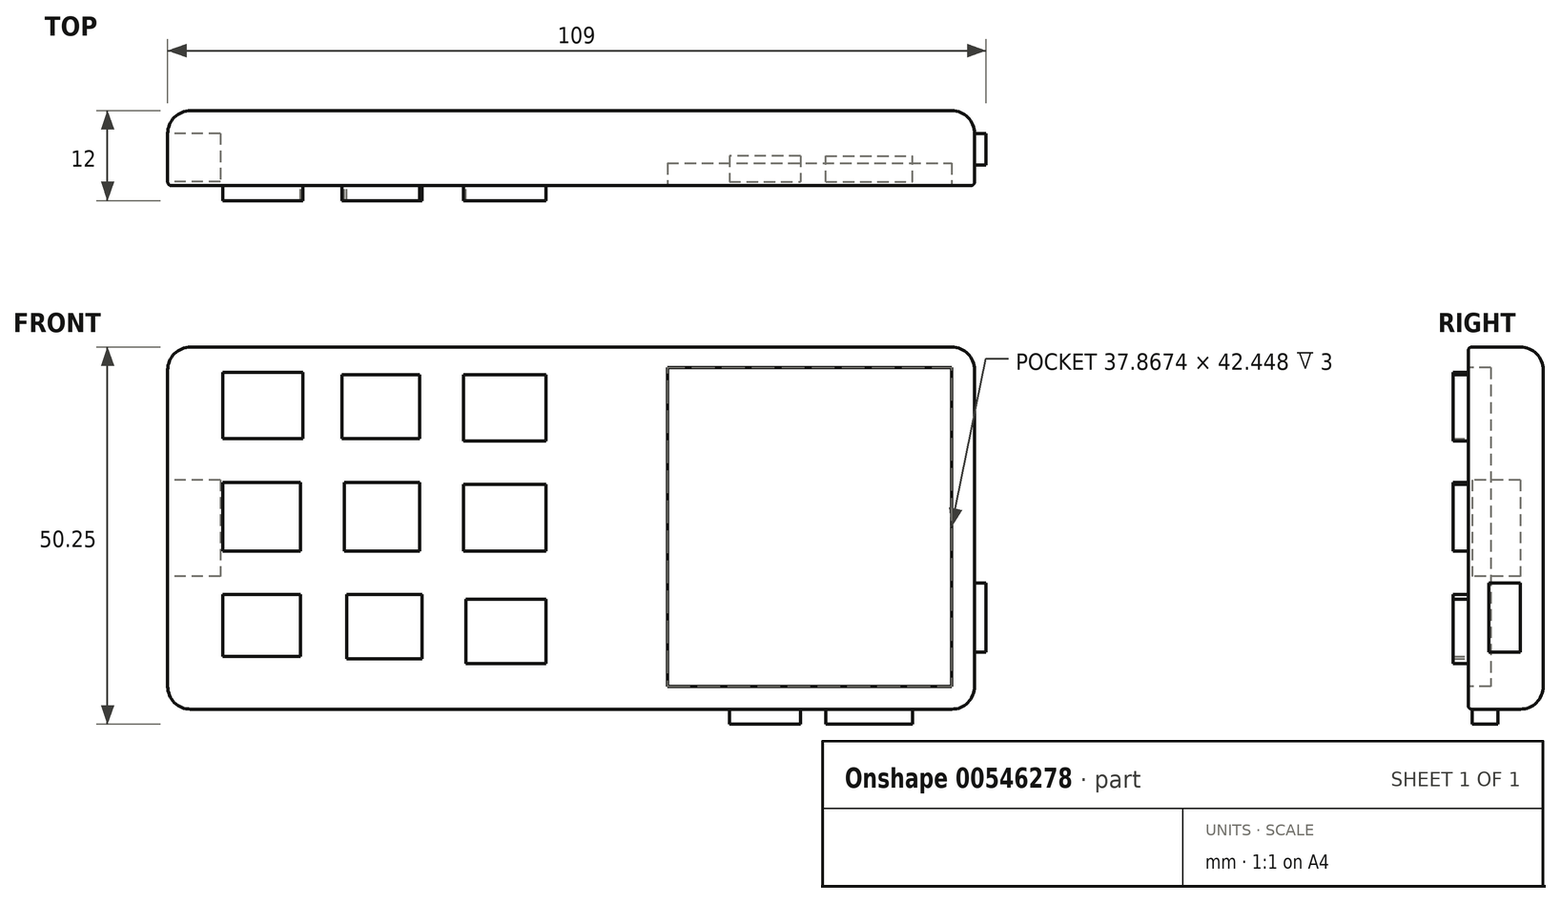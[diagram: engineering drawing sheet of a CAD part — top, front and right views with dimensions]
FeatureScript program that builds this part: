
annotation { "Feature Type Name" : "Feature", "Feature Type Description" : "" }
export const myFeature = defineFeature(function(context is Context, id is Id, definition is map)
    precondition{}
    {
        {
            var Q0;
            Q0=qCreatedBy(makeId("Front.planeOp"),FACE);
            var sketch = newSketch(context, id + "F0", { "sketchPlane" : qUnion([Q0])});
            skLineSegment(sketch, "E0.bottom", {"start": v(-50.39, 27.18) * mm, "end": v(57.1, 27.18) * mm});
            skLineSegment(sketch, "E0.top", {"start": v(-50.39, -21.07) * mm, "end": v(57.1, -21.07) * mm});
            skLineSegment(sketch, "E0.left", {"start": v(-50.39, 27.18) * mm, "end": v(-50.39, -21.07) * mm});
            skLineSegment(sketch, "E0.right", {"start": v(57.1, 27.18) * mm, "end": v(57.1, -21.07) * mm});
            skSolve(sketch);
        }
        {
            var Q0;
            Q0=makeQuery(id+"F0.imprint","IMPRINT",FACE,{"disambiguationData":[TD([[makeQuery(id+"F0.imprint","IMPRINT",EDGE,{"derivedFrom":sQuery(id+"F0.wireOp",EDGE,"E0.bottom")}),-1.0]])]});
            extrude(context, id + "F1", {"entities" : qUnion([Q0]), "oppositeDirection" : true, "depth" : 10 * mm, "offsetDistance" : 25.4 * mm});
        }
        {
            var Q0;
            Q0=makeQuery(id+"F1.opExtrude","CAP_FACE",FACE,{"disambiguationData":[OSD([sQuery(id+"F0.wireOp",EDGE,"E0.bottom"),sQuery(id+"F0.wireOp",EDGE,"E0.top"),sQuery(id+"F0.wireOp",EDGE,"E0.left"),sQuery(id+"F0.wireOp",EDGE,"E0.right")])],"isStart":true});
            var sketch = newSketch(context, id + "F2", { "sketchPlane" : qUnion([Q0])});
            skLineSegment(sketch, "E1.bottom", {"start": v(16.19, 24.43) * mm, "end": v(54.05, 24.43) * mm});
            skLineSegment(sketch, "E1.top", {"start": v(16.19, -18.02) * mm, "end": v(54.05, -18.02) * mm});
            skLineSegment(sketch, "E1.left", {"start": v(16.19, 24.43) * mm, "end": v(16.19, -18.02) * mm});
            skLineSegment(sketch, "E1.right", {"start": v(54.05, 24.43) * mm, "end": v(54.05, -18.02) * mm});
            skSolve(sketch);
        }
        {
            var Q0;
            Q0=makeQuery(id+"F2.imprint","IMPRINT",FACE,{"disambiguationData":[TD([[makeQuery(id+"F2.imprint","IMPRINT",EDGE,{"derivedFrom":sQuery(id+"F2.wireOp",EDGE,"E1.bottom")}),-1.0]])]});
            extrude(context, id + "F3", {"entities" : qUnion([Q0]), "operationType" : NewBodyOperationType.REMOVE, "oppositeDirection" : true, "depth" : 3 * mm, "offsetDistance" : 25.4 * mm});
        }
        {
            var Q0;
            Q0=makeQuery(id+"F1.opExtrude","CAP_FACE",FACE,{"disambiguationData":[OSD([sQuery(id+"F0.wireOp",EDGE,"E0.bottom"),sQuery(id+"F0.wireOp",EDGE,"E0.top"),sQuery(id+"F0.wireOp",EDGE,"E0.left"),sQuery(id+"F0.wireOp",EDGE,"E0.right")])],"isStart":true});
            var sketch = newSketch(context, id + "F4", { "sketchPlane" : qUnion([Q0])});
            skLineSegment(sketch, "E2.bottom", {"start": v(0, 23.51) * mm, "end": v(-11, 23.51) * mm});
            skLineSegment(sketch, "E2.top", {"start": v(0, 14.66) * mm, "end": v(-11, 14.66) * mm});
            skLineSegment(sketch, "E2.left", {"start": v(0, 23.51) * mm, "end": v(0, 14.66) * mm});
            skLineSegment(sketch, "E2.right", {"start": v(-11, 23.51) * mm, "end": v(-11, 14.66) * mm});
            skLineSegment(sketch, "E3.bottom", {"start": v(0, 8.55) * mm, "end": v(-11, 8.55) * mm});
            skLineSegment(sketch, "E3.top", {"start": v(0, 0) * mm, "end": v(-11, 0) * mm});
            skLineSegment(sketch, "E3.left", {"start": v(0, 8.55) * mm, "end": v(0, 0) * mm});
            skLineSegment(sketch, "E3.right", {"start": v(-11, 8.55) * mm, "end": v(-11, 0) * mm});
            skLineSegment(sketch, "E4.bottom", {"start": v(0, -6.72) * mm, "end": v(-11, -6.72) * mm});
            skLineSegment(sketch, "E4.top", {"start": v(0, -14.96) * mm, "end": v(-11, -14.96) * mm});
            skLineSegment(sketch, "E4.left", {"start": v(0, -6.72) * mm, "end": v(0, -14.96) * mm});
            skLineSegment(sketch, "E4.right", {"start": v(-11, -6.72) * mm, "end": v(-11, -14.96) * mm});
            skLineSegment(sketch, "E5.bottom", {"start": v(-17.1, -6.72) * mm, "end": v(-28.1, -6.72) * mm});
            skLineSegment(sketch, "E5.top", {"start": v(-17.1, -14.96) * mm, "end": v(-28.1, -14.96) * mm});
            skLineSegment(sketch, "E5.left", {"start": v(-17.1, -6.72) * mm, "end": v(-17.1, -14.96) * mm});
            skLineSegment(sketch, "E5.right", {"start": v(-28.1, -6.72) * mm, "end": v(-28.1, -14.96) * mm});
            skLineSegment(sketch, "E6.bottom", {"start": v(-16.8, 0) * mm, "end": v(-28.1, 0) * mm});
            skLineSegment(sketch, "E6.top", {"start": v(-16.8, 8.55) * mm, "end": v(-28.1, 8.55) * mm});
            skLineSegment(sketch, "E6.left", {"start": v(-16.8, 0) * mm, "end": v(-16.8, 8.55) * mm});
            skLineSegment(sketch, "E6.right", {"start": v(-28.1, 0) * mm, "end": v(-28.1, 8.55) * mm});
            skLineSegment(sketch, "E7.bottom", {"start": v(-17.1, 14.66) * mm, "end": v(-28.1, 14.66) * mm});
            skLineSegment(sketch, "E7.top", {"start": v(-17.1, 23.82) * mm, "end": v(-28.1, 23.82) * mm});
            skLineSegment(sketch, "E7.left", {"start": v(-17.1, 14.66) * mm, "end": v(-17.1, 23.82) * mm});
            skLineSegment(sketch, "E7.right", {"start": v(-28.1, 14.66) * mm, "end": v(-28.1, 23.82) * mm});
            skLineSegment(sketch, "E8.bottom", {"start": v(-34.2, 23.82) * mm, "end": v(-44.59, 23.82) * mm});
            skLineSegment(sketch, "E8.top", {"start": v(-34.2, 14.66) * mm, "end": v(-44.59, 14.66) * mm});
            skLineSegment(sketch, "E8.left", {"start": v(-34.2, 23.82) * mm, "end": v(-34.2, 14.66) * mm});
            skLineSegment(sketch, "E8.right", {"start": v(-44.59, 23.82) * mm, "end": v(-44.59, 14.66) * mm});
            skLineSegment(sketch, "E9.bottom", {"start": v(-34.5, 8.55) * mm, "end": v(-44.59, 8.55) * mm});
            skLineSegment(sketch, "E9.top", {"start": v(-34.5, 0) * mm, "end": v(-44.59, 0) * mm});
            skLineSegment(sketch, "E9.left", {"start": v(-34.5, 8.55) * mm, "end": v(-34.5, 0) * mm});
            skLineSegment(sketch, "E9.right", {"start": v(-44.59, 8.55) * mm, "end": v(-44.59, 0) * mm});
            skLineSegment(sketch, "E10.bottom", {"start": v(-34.81, -6.72) * mm, "end": v(-44.59, -6.72) * mm});
            skLineSegment(sketch, "E10.top", {"start": v(-34.81, -14.96) * mm, "end": v(-44.59, -14.96) * mm});
            skLineSegment(sketch, "E10.left", {"start": v(-34.81, -6.72) * mm, "end": v(-34.81, -14.96) * mm});
            skLineSegment(sketch, "E10.right", {"start": v(-44.59, -6.72) * mm, "end": v(-44.59, -14.96) * mm});
            skSolve(sketch);
        }
        {
            var Q0;
            Q0=makeQuery(id+"F4.imprint","IMPRINT",FACE,{"disambiguationData":[TD([[makeQuery(id+"F4.imprint","IMPRINT",EDGE,{"derivedFrom":sQuery(id+"F4.wireOp",EDGE,"E2.bottom")}),1.0]])]});
            extrude(context, id + "F5", {"entities" : qUnion([Q0]), "operationType" : NewBodyOperationType.ADD, "depth" : 2 * mm, "offsetDistance" : 25.4 * mm});
        }
        {
            var Q0;
            Q0=makeQuery(id+"F1.opExtrude","CAP_FACE",FACE,{"disambiguationData":[OSD([sQuery(id+"F0.wireOp",EDGE,"E0.bottom"),sQuery(id+"F0.wireOp",EDGE,"E0.top"),sQuery(id+"F0.wireOp",EDGE,"E0.left"),sQuery(id+"F0.wireOp",EDGE,"E0.right")])],"isStart":true});
            var sketch = newSketch(context, id + "F6", { "sketchPlane" : qUnion([Q0])});
            skLineSegment(sketch, "E11.bottom", {"start": v(-11, 8.86) * mm, "end": v(0, 8.86) * mm});
            skLineSegment(sketch, "E11.top", {"start": v(-11, 0) * mm, "end": v(0, 0) * mm});
            skLineSegment(sketch, "E11.left", {"start": v(-11, 8.86) * mm, "end": v(-11, 0) * mm});
            skLineSegment(sketch, "E11.right", {"start": v(0, 8.86) * mm, "end": v(0, 0) * mm});
            skSolve(sketch);
        }
        {
            var Q0;
            Q0=makeQuery(id+"F6.imprint","IMPRINT",FACE,{"disambiguationData":[TD([[makeQuery(id+"F6.imprint","IMPRINT",EDGE,{"derivedFrom":sQuery(id+"F6.wireOp",EDGE,"E11.bottom")}),-1.0]])]});
            extrude(context, id + "F7", {"entities" : qUnion([Q0]), "operationType" : NewBodyOperationType.ADD, "depth" : 2 * mm, "offsetDistance" : 25.4 * mm});
        }
        {
            var Q0;
            Q0=makeQuery(id+"F1.opExtrude","CAP_FACE",FACE,{"disambiguationData":[OSD([sQuery(id+"F0.wireOp",EDGE,"E0.bottom"),sQuery(id+"F0.wireOp",EDGE,"E0.top"),sQuery(id+"F0.wireOp",EDGE,"E0.left"),sQuery(id+"F0.wireOp",EDGE,"E0.right")])],"isStart":true});
            var sketch = newSketch(context, id + "F8", { "sketchPlane" : qUnion([Q0])});
            skLineSegment(sketch, "E12.bottom", {"start": v(0, -6.41) * mm, "end": v(-10.69, -6.41) * mm});
            skLineSegment(sketch, "E12.top", {"start": v(0, -14.96) * mm, "end": v(-10.69, -14.96) * mm});
            skLineSegment(sketch, "E12.left", {"start": v(0, -6.41) * mm, "end": v(0, -14.96) * mm});
            skLineSegment(sketch, "E12.right", {"start": v(-10.69, -6.41) * mm, "end": v(-10.69, -14.96) * mm});
            skSolve(sketch);
        }
        {
            var Q0;
            Q0=makeQuery(id+"F8.imprint","IMPRINT",FACE,{"disambiguationData":[TD([[makeQuery(id+"F8.imprint","IMPRINT",EDGE,{"derivedFrom":sQuery(id+"F8.wireOp",EDGE,"E12.bottom")}),1.0]])]});
            extrude(context, id + "F9", {"entities" : qUnion([Q0]), "operationType" : NewBodyOperationType.ADD, "depth" : 2 * mm, "offsetDistance" : 25.4 * mm});
        }
        {
            var Q0;
            Q0=makeQuery(id+"F1.opExtrude","CAP_FACE",FACE,{"disambiguationData":[OSD([sQuery(id+"F0.wireOp",EDGE,"E0.bottom"),sQuery(id+"F0.wireOp",EDGE,"E0.top"),sQuery(id+"F0.wireOp",EDGE,"E0.left"),sQuery(id+"F0.wireOp",EDGE,"E0.right")])],"isStart":true});
            var sketch = newSketch(context, id + "F10", { "sketchPlane" : qUnion([Q0])});
            skLineSegment(sketch, "E13.bottom", {"start": v(-16.8, 23.51) * mm, "end": v(-27.18, 23.51) * mm});
            skLineSegment(sketch, "E13.top", {"start": v(-16.8, 14.96) * mm, "end": v(-27.18, 14.96) * mm});
            skLineSegment(sketch, "E13.left", {"start": v(-16.8, 23.51) * mm, "end": v(-16.8, 14.96) * mm});
            skLineSegment(sketch, "E13.right", {"start": v(-27.18, 23.51) * mm, "end": v(-27.18, 14.96) * mm});
            skSolve(sketch);
        }
        {
            var Q0;
            Q0=makeQuery(id+"F10.imprint","IMPRINT",FACE,{"disambiguationData":[TD([[makeQuery(id+"F10.imprint","IMPRINT",EDGE,{"derivedFrom":sQuery(id+"F10.wireOp",EDGE,"E13.bottom")}),1.0]])]});
            extrude(context, id + "F11", {"entities" : qUnion([Q0]), "operationType" : NewBodyOperationType.ADD, "depth" : 2 * mm, "offsetDistance" : 25.4 * mm});
        }
        {
            var Q0;
            Q0=makeQuery(id+"F1.opExtrude","CAP_FACE",FACE,{"disambiguationData":[OSD([sQuery(id+"F0.wireOp",EDGE,"E0.bottom"),sQuery(id+"F0.wireOp",EDGE,"E0.top"),sQuery(id+"F0.wireOp",EDGE,"E0.left"),sQuery(id+"F0.wireOp",EDGE,"E0.right")])],"isStart":true});
            var sketch = newSketch(context, id + "F12", { "sketchPlane" : qUnion([Q0])});
            skLineSegment(sketch, "E14.bottom", {"start": v(-16.8, 0) * mm, "end": v(-26.87, 0) * mm});
            skLineSegment(sketch, "E14.top", {"start": v(-16.8, 9.16) * mm, "end": v(-26.87, 9.16) * mm});
            skLineSegment(sketch, "E14.left", {"start": v(-16.8, 0) * mm, "end": v(-16.8, 9.16) * mm});
            skLineSegment(sketch, "E14.right", {"start": v(-26.87, 0) * mm, "end": v(-26.87, 9.16) * mm});
            skSolve(sketch);
        }
        {
            var Q0;
            Q0=makeQuery(id+"F12.imprint","IMPRINT",FACE,{"disambiguationData":[TD([[makeQuery(id+"F12.imprint","IMPRINT",EDGE,{"derivedFrom":sQuery(id+"F12.wireOp",EDGE,"E14.bottom")}),-1.0]])]});
            extrude(context, id + "F13", {"entities" : qUnion([Q0]), "operationType" : NewBodyOperationType.ADD, "depth" : 2 * mm, "offsetDistance" : 25.4 * mm});
        }
        {
            var Q0;
            Q0=makeQuery(id+"F1.opExtrude","CAP_FACE",FACE,{"disambiguationData":[OSD([sQuery(id+"F0.wireOp",EDGE,"E0.bottom"),sQuery(id+"F0.wireOp",EDGE,"E0.top"),sQuery(id+"F0.wireOp",EDGE,"E0.left"),sQuery(id+"F0.wireOp",EDGE,"E0.right")])],"isStart":true});
            var sketch = newSketch(context, id + "F14", { "sketchPlane" : qUnion([Q0])});
            skLineSegment(sketch, "E15.bottom", {"start": v(-16.5, -5.8) * mm, "end": v(-26.57, -5.8) * mm});
            skLineSegment(sketch, "E15.top", {"start": v(-16.5, -14.35) * mm, "end": v(-26.57, -14.35) * mm});
            skLineSegment(sketch, "E15.left", {"start": v(-16.5, -5.8) * mm, "end": v(-16.5, -14.35) * mm});
            skLineSegment(sketch, "E15.right", {"start": v(-26.57, -5.8) * mm, "end": v(-26.57, -14.35) * mm});
            skSolve(sketch);
        }
        {
            var Q0;
            Q0=makeQuery(id+"F14.imprint","IMPRINT",FACE,{"disambiguationData":[TD([[makeQuery(id+"F14.imprint","IMPRINT",EDGE,{"derivedFrom":sQuery(id+"F14.wireOp",EDGE,"E15.bottom")}),1.0]])]});
            extrude(context, id + "F15", {"entities" : qUnion([Q0]), "operationType" : NewBodyOperationType.ADD, "depth" : 2 * mm, "offsetDistance" : 25.4 * mm});
        }
        {
            var Q0;
            Q0=makeQuery(id+"F1.opExtrude","CAP_FACE",FACE,{"disambiguationData":[OSD([sQuery(id+"F0.wireOp",EDGE,"E0.bottom"),sQuery(id+"F0.wireOp",EDGE,"E0.top"),sQuery(id+"F0.wireOp",EDGE,"E0.left"),sQuery(id+"F0.wireOp",EDGE,"E0.right")])],"isStart":true});
            var sketch = newSketch(context, id + "F16", { "sketchPlane" : qUnion([Q0])});
            skLineSegment(sketch, "E16.bottom", {"start": v(-32.37, 14.96) * mm, "end": v(-43.06, 14.96) * mm});
            skLineSegment(sketch, "E16.top", {"start": v(-32.37, 23.82) * mm, "end": v(-43.06, 23.82) * mm});
            skLineSegment(sketch, "E16.left", {"start": v(-32.37, 14.96) * mm, "end": v(-32.37, 23.82) * mm});
            skLineSegment(sketch, "E16.right", {"start": v(-43.06, 14.96) * mm, "end": v(-43.06, 23.82) * mm});
            skSolve(sketch);
        }
        {
            var Q0;
            Q0=makeQuery(id+"F16.imprint","IMPRINT",FACE,{"disambiguationData":[TD([[makeQuery(id+"F16.imprint","IMPRINT",EDGE,{"derivedFrom":sQuery(id+"F16.wireOp",EDGE,"E16.bottom")}),-1.0]])]});
            extrude(context, id + "F17", {"entities" : qUnion([Q0]), "operationType" : NewBodyOperationType.ADD, "depth" : 2 * mm, "offsetDistance" : 25.4 * mm});
        }
        {
            var Q0;
            Q0=makeQuery(id+"F1.opExtrude","CAP_FACE",FACE,{"disambiguationData":[OSD([sQuery(id+"F0.wireOp",EDGE,"E0.bottom"),sQuery(id+"F0.wireOp",EDGE,"E0.top"),sQuery(id+"F0.wireOp",EDGE,"E0.left"),sQuery(id+"F0.wireOp",EDGE,"E0.right")])],"isStart":true});
            var sketch = newSketch(context, id + "F18", { "sketchPlane" : qUnion([Q0])});
            skLineSegment(sketch, "E17.bottom", {"start": v(-32.68, 9.16) * mm, "end": v(-43.06, 9.16) * mm});
            skLineSegment(sketch, "E17.top", {"start": v(-32.68, 0) * mm, "end": v(-43.06, 0) * mm});
            skLineSegment(sketch, "E17.left", {"start": v(-32.68, 9.16) * mm, "end": v(-32.68, 0) * mm});
            skLineSegment(sketch, "E17.right", {"start": v(-43.06, 9.16) * mm, "end": v(-43.06, 0) * mm});
            skSolve(sketch);
        }
        {
            var Q0;
            Q0=makeQuery(id+"F18.imprint","IMPRINT",FACE,{"disambiguationData":[TD([[makeQuery(id+"F18.imprint","IMPRINT",EDGE,{"derivedFrom":sQuery(id+"F18.wireOp",EDGE,"E17.bottom")}),1.0]])]});
            extrude(context, id + "F19", {"entities" : qUnion([Q0]), "operationType" : NewBodyOperationType.ADD, "depth" : 2 * mm, "offsetDistance" : 25.4 * mm});
        }
        {
            var Q0;
            Q0=makeQuery(id+"F1.opExtrude","CAP_FACE",FACE,{"disambiguationData":[OSD([sQuery(id+"F0.wireOp",EDGE,"E0.bottom"),sQuery(id+"F0.wireOp",EDGE,"E0.top"),sQuery(id+"F0.wireOp",EDGE,"E0.left"),sQuery(id+"F0.wireOp",EDGE,"E0.right")])],"isStart":true});
            var sketch = newSketch(context, id + "F20", { "sketchPlane" : qUnion([Q0])});
            skPoint(sketch, "E18.oppositeSnap0", {"position": v(-43.06, 19.4) * mm});
            skLineSegment(sketch, "E18.bottom", {"start": v(-32.68, -5.8) * mm, "end": v(-43.06, -5.8) * mm});
            skLineSegment(sketch, "E18.top", {"start": v(-32.68, -14.05) * mm, "end": v(-43.06, -14.05) * mm});
            skLineSegment(sketch, "E18.left", {"start": v(-32.68, -5.8) * mm, "end": v(-32.68, -14.05) * mm});
            skLineSegment(sketch, "E18.right", {"start": v(-43.06, -5.8) * mm, "end": v(-43.06, -14.05) * mm});
            skSolve(sketch);
        }
        {
            var Q0;
            Q0=makeQuery(id+"F20.imprint","IMPRINT",FACE,{"disambiguationData":[TD([[makeQuery(id+"F20.imprint","IMPRINT",EDGE,{"derivedFrom":sQuery(id+"F20.wireOp",EDGE,"E18.bottom")}),1.0]])]});
            extrude(context, id + "F21", {"entities" : qUnion([Q0]), "operationType" : NewBodyOperationType.ADD, "depth" : 2 * mm, "offsetDistance" : 25.4 * mm});
        }
        {
            var Q0;
            Q0=makeQuery(id+"F1.opExtrude","SWEPT_EDGE",EDGE,{"disambiguationData":[OSD([sQuery(id+"F0.wireOp",EDGE,"E0.top"),sQuery(id+"F0.wireOp",EDGE,"E0.left")])]});
            fillet(context, id + "F22", {"entities" : qUnion([Q0]), "radius" : 3.05 * mm, "tangentPropagation" : true, "allowEdgeOverflow" : false});
        }
        {
            var Q0;
            Q0=makeQuery(id+"F1.opExtrude","SWEPT_EDGE",EDGE,{"disambiguationData":[OSD([sQuery(id+"F0.wireOp",EDGE,"E0.top"),sQuery(id+"F0.wireOp",EDGE,"E0.right")])]});
            fillet(context, id + "F23", {"entities" : qUnion([Q0]), "radius" : 3.05 * mm, "tangentPropagation" : true, "allowEdgeOverflow" : false});
        }
        {
            var Q0;
            Q0=makeQuery(id+"F1.opExtrude","SWEPT_EDGE",EDGE,{"disambiguationData":[OSD([sQuery(id+"F0.wireOp",EDGE,"E0.bottom"),sQuery(id+"F0.wireOp",EDGE,"E0.right")])]});
            fillet(context, id + "F24", {"entities" : qUnion([Q0]), "radius" : 3.05 * mm, "tangentPropagation" : true, "allowEdgeOverflow" : false});
        }
        {
            var Q0;
            Q0=makeQuery(id+"F1.opExtrude","SWEPT_EDGE",EDGE,{"disambiguationData":[OSD([sQuery(id+"F0.wireOp",EDGE,"E0.bottom"),sQuery(id+"F0.wireOp",EDGE,"E0.left")])]});
            fillet(context, id + "F25", {"entities" : qUnion([Q0]), "radius" : 3.05 * mm, "tangentPropagation" : true, "allowEdgeOverflow" : false});
        }
        {
            var Q0;
            Q0=makeQuery(id+"F1.opExtrude","CAP_EDGE",EDGE,{"disambiguationData":[OSD([sQuery(id+"F0.wireOp",EDGE,"E0.bottom")])],"isStart":false});
            fillet(context, id + "F26", {"entities" : qUnion([Q0]), "radius" : 3.05 * mm, "tangentPropagation" : true, "allowEdgeOverflow" : false});
        }
        {
            var Q0;
            Q0=makeQuery(id+"F1.opExtrude","CAP_EDGE",EDGE,{"disambiguationData":[OSD([sQuery(id+"F0.wireOp",EDGE,"E0.bottom")])],"isStart":true});
            fillet(context, id + "F27", {"entities" : qUnion([Q0]), "radius" : 0.5 * mm, "tangentPropagation" : true, "allowEdgeOverflow" : false});
        }
        {
            var Q0;
            Q0=makeQuery(id+"F1.opExtrude","SWEPT_FACE",FACE,{"disambiguationData":[OSD([sQuery(id+"F0.wireOp",EDGE,"E0.left")])]});
            var sketch = newSketch(context, id + "F28", { "sketchPlane" : qUnion([Q0])});
            skLineSegment(sketch, "E19.bottom", {"start": v(-6.95, 9.47) * mm, "end": v(-0.5, 9.47) * mm});
            skLineSegment(sketch, "E19.top", {"start": v(-6.95, -3.36) * mm, "end": v(-0.5, -3.36) * mm});
            skLineSegment(sketch, "E19.left", {"start": v(-6.95, 9.47) * mm, "end": v(-6.95, -3.36) * mm});
            skLineSegment(sketch, "E19.right", {"start": v(-0.5, 9.47) * mm, "end": v(-0.5, -3.36) * mm});
            skSolve(sketch);
        }
        {
            var Q0;
            Q0=makeQuery(id+"F28.imprint","IMPRINT",FACE,{"disambiguationData":[TD([[makeQuery(id+"F28.imprint","IMPRINT",EDGE,{"derivedFrom":sQuery(id+"F28.wireOp",EDGE,"E19.bottom")}),-1.0]])]});
            extrude(context, id + "F29", {"entities" : qUnion([Q0]), "operationType" : NewBodyOperationType.REMOVE, "oppositeDirection" : true, "depth" : 7 * mm, "offsetDistance" : 25.4 * mm});
        }
        {
            var Q0;
            Q0=makeQuery(id+"F1.opExtrude","SWEPT_FACE",FACE,{"disambiguationData":[OSD([sQuery(id+"F0.wireOp",EDGE,"E0.top")])]});
            var sketch = newSketch(context, id + "F30", { "sketchPlane" : qUnion([Q0])});
            skLineSegment(sketch, "E20.bottom", {"start": v(37.26, -0.5) * mm, "end": v(48.86, -0.5) * mm});
            skLineSegment(sketch, "E20.top", {"start": v(37.26, -3.97) * mm, "end": v(48.86, -3.97) * mm});
            skLineSegment(sketch, "E20.left", {"start": v(37.26, -0.5) * mm, "end": v(37.26, -3.97) * mm});
            skLineSegment(sketch, "E20.right", {"start": v(48.86, -0.5) * mm, "end": v(48.86, -3.97) * mm});
            skSolve(sketch);
        }
        {
            var Q0;
            Q0=makeQuery(id+"F30.imprint","IMPRINT",FACE,{"disambiguationData":[TD([[makeQuery(id+"F30.imprint","IMPRINT",EDGE,{"derivedFrom":sQuery(id+"F30.wireOp",EDGE,"E20.bottom")}),1.0]])]});
            extrude(context, id + "F31", {"entities" : qUnion([Q0]), "operationType" : NewBodyOperationType.ADD, "depth" : 2 * mm, "offsetDistance" : 25.4 * mm});
        }
        {
            var Q0;
            Q0=makeQuery(id+"F1.opExtrude","SWEPT_FACE",FACE,{"disambiguationData":[OSD([sQuery(id+"F0.wireOp",EDGE,"E0.top")])]});
            var sketch = newSketch(context, id + "F32", { "sketchPlane" : qUnion([Q0])});
            skLineSegment(sketch, "E21.bottom", {"start": v(33.9, -3.97) * mm, "end": v(24.43, -3.97) * mm});
            skLineSegment(sketch, "E21.top", {"start": v(33.9, -0.5) * mm, "end": v(24.43, -0.5) * mm});
            skLineSegment(sketch, "E21.left", {"start": v(33.9, -3.97) * mm, "end": v(33.9, -0.5) * mm});
            skLineSegment(sketch, "E21.right", {"start": v(24.43, -3.97) * mm, "end": v(24.43, -0.5) * mm});
            skSolve(sketch);
        }
        {
            var Q0;
            Q0=makeQuery(id+"F32.imprint","IMPRINT",FACE,{"disambiguationData":[TD([[makeQuery(id+"F32.imprint","IMPRINT",EDGE,{"derivedFrom":sQuery(id+"F32.wireOp",EDGE,"E21.bottom")}),-1.0]])]});
            extrude(context, id + "F33", {"entities" : qUnion([Q0]), "operationType" : NewBodyOperationType.ADD, "depth" : 2 * mm, "offsetDistance" : 25.4 * mm});
        }
        {
            var Q0;
            Q0=makeQuery(id+"F1.opExtrude","SWEPT_FACE",FACE,{"disambiguationData":[OSD([sQuery(id+"F0.wireOp",EDGE,"E0.right")])]});
            var sketch = newSketch(context, id + "F34", { "sketchPlane" : qUnion([Q0])});
            skLineSegment(sketch, "E22.bottom", {"start": v(2.75, -4.28) * mm, "end": v(6.95, -4.28) * mm});
            skLineSegment(sketch, "E22.top", {"start": v(2.75, -13.44) * mm, "end": v(6.95, -13.44) * mm});
            skLineSegment(sketch, "E22.left", {"start": v(2.75, -4.28) * mm, "end": v(2.75, -13.44) * mm});
            skLineSegment(sketch, "E22.right", {"start": v(6.95, -4.28) * mm, "end": v(6.95, -13.44) * mm});
            skSolve(sketch);
        }
        {
            var Q0;
            Q0=makeQuery(id+"F34.imprint","IMPRINT",FACE,{"disambiguationData":[TD([[makeQuery(id+"F34.imprint","IMPRINT",EDGE,{"derivedFrom":sQuery(id+"F34.wireOp",EDGE,"E22.bottom")}),-1.0]])]});
            extrude(context, id + "F35", {"entities" : qUnion([Q0]), "operationType" : NewBodyOperationType.ADD, "depth" : 1.5 * mm, "offsetDistance" : 25.4 * mm});
        }
    });
